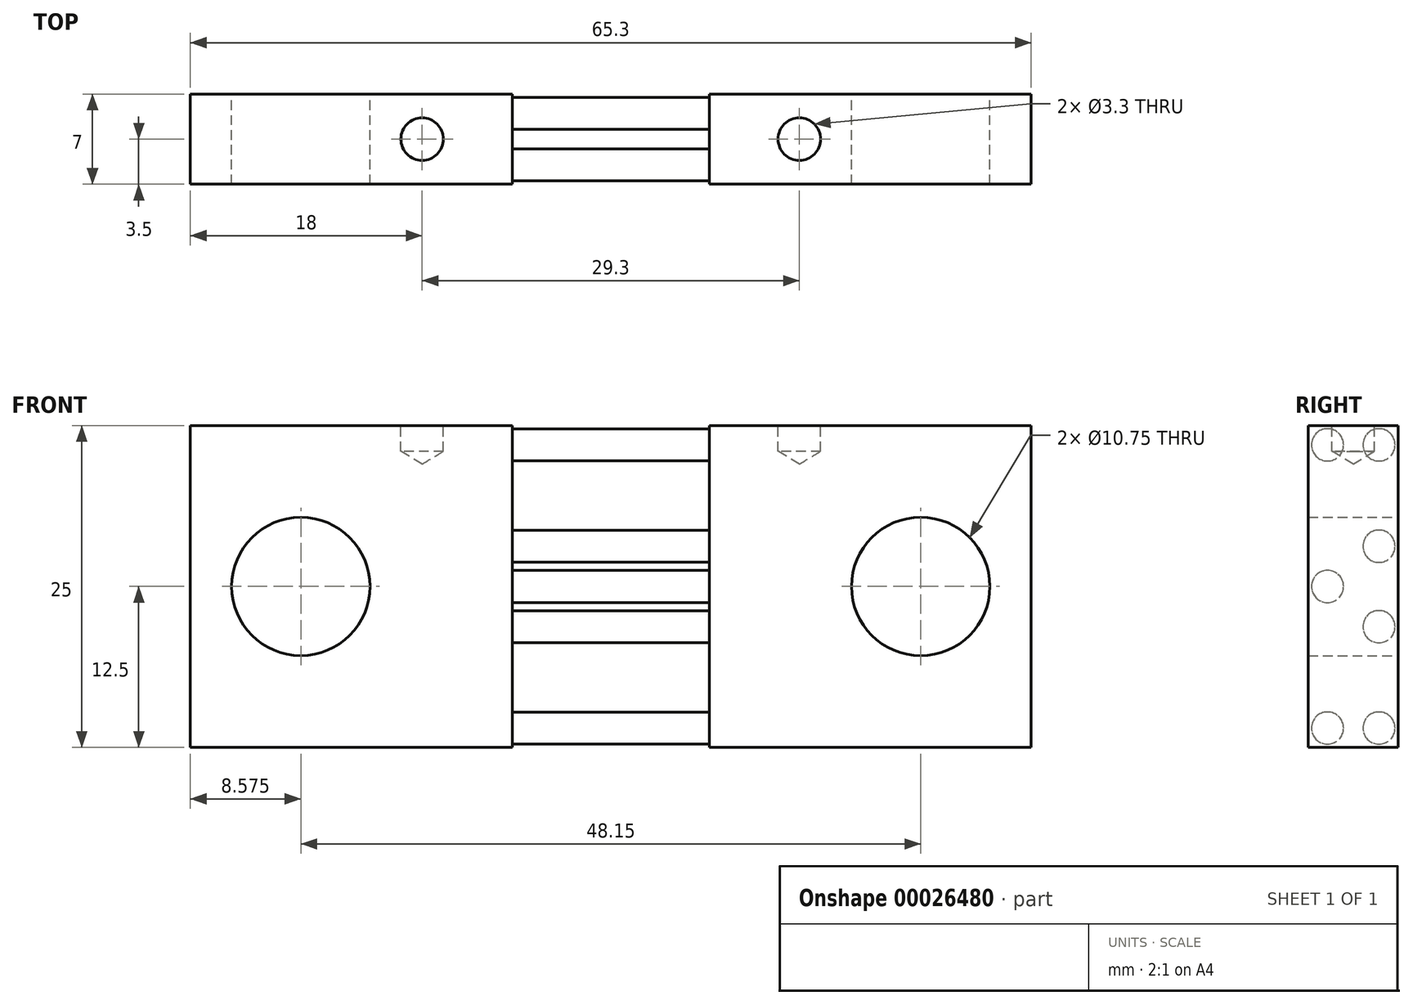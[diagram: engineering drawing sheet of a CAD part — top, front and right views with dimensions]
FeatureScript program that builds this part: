
annotation { "Feature Type Name" : "Feature", "Feature Type Description" : "" }
export const myFeature = defineFeature(function(context is Context, id is Id, definition is map)
    precondition{}
    {
        {
            var Q0;
            Q0=qCreatedBy(makeId("Front.planeOp"),FACE);
            var sketch = newSketch(context, id + "F0", { "sketchPlane" : qUnion([Q0])});
            skLineSegment(sketch, "E0.rect.bottom", {"start": v(-32.65, -12.5) * mm, "end": v(-7.65, -12.5) * mm});
            skLineSegment(sketch, "E0.rect.top", {"start": v(-32.65, 12.5) * mm, "end": v(-7.65, 12.5) * mm});
            skLineSegment(sketch, "E0.rect.left", {"start": v(-32.65, -12.5) * mm, "end": v(-32.65, 12.5) * mm});
            skLineSegment(sketch, "E0.rect.right", {"start": v(-7.65, -12.5) * mm, "end": v(-7.65, 12.5) * mm});
            skPoint(sketch, "E0.rect.middle", {"position": v(-20.15, 0) * mm});
            skLineSegment(sketch, "E1.rect.bottom", {"start": v(32.65, -12.5) * mm, "end": v(7.65, -12.5) * mm});
            skLineSegment(sketch, "E1.rect.top", {"start": v(32.65, 12.5) * mm, "end": v(7.65, 12.5) * mm});
            skLineSegment(sketch, "E1.rect.left", {"start": v(32.65, -12.5) * mm, "end": v(32.65, 12.5) * mm});
            skLineSegment(sketch, "E1.rect.right", {"start": v(7.65, -12.5) * mm, "end": v(7.65, 12.5) * mm});
            skPoint(sketch, "E1.rect.middle", {"position": v(20.15, 0) * mm});
            skLineSegment(sketch, "E2", {"start": v(-7.65, 12.5) * mm, "end": v(7.65, 12.5) * mm, "construction": true});
            skCircle(sketch, "E3", {"center": v(-24.07, 0) * mm, "radius": 5.38 * mm});
            skCircle(sketch, "E4", {"center": v(24.08, 0) * mm, "radius": 5.38 * mm});
            skSolve(sketch);
        }
        {
            var Q0;
            Q0=makeQuery(id+"F0.imprint","IMPRINT",FACE,{"disambiguationData":[TD([[makeQuery(id+"F0.imprint","IMPRINT",EDGE,{"derivedFrom":sQuery(id+"F0.wireOp",EDGE,"E0.rect.bottom")}),1.0]])]});
            var Q1;
            Q1=makeQuery(id+"F0.imprint","IMPRINT",FACE,{"disambiguationData":[TD([[makeQuery(id+"F0.imprint","IMPRINT",EDGE,{"derivedFrom":sQuery(id+"F0.wireOp",EDGE,"E1.rect.bottom")}),-1.0]])]});
            extrude(context, id + "F1", {"entities" : qUnion([Q0, Q1]), "endBound" : BoundingType.SYMMETRIC, "depth" : 7 * mm});
        }
        {
            var Q0;
            Q0=makeQuery(id+"F1.opExtrude","SWEPT_FACE",FACE,{"disambiguationData":[OSD([sQuery(id+"F0.wireOp",EDGE,"E0.rect.right")])]});
            var sketch = newSketch(context, id + "F2", { "sketchPlane" : qUnion([Q0])});
            skCircle(sketch, "E5", {"center": v(-2, 11) * mm, "radius": 1.25 * mm});
            skCircle(sketch, "E6", {"center": v(-2, 0) * mm, "radius": 1.25 * mm});
            skCircle(sketch, "E7", {"center": v(-2, -11) * mm, "radius": 1.25 * mm});
            skCircle(sketch, "E8", {"center": v(2, 11) * mm, "radius": 1.25 * mm});
            skCircle(sketch, "E9", {"center": v(2, 3.13) * mm, "radius": 1.25 * mm});
            skCircle(sketch, "E10", {"center": v(2, -3.12) * mm, "radius": 1.25 * mm});
            skCircle(sketch, "E11", {"center": v(2, -11) * mm, "radius": 1.25 * mm});
            skLineSegment(sketch, "E12", {"start": v(-3.5, 0) * mm, "end": v(3.5, 0) * mm, "construction": true});
            skSolve(sketch);
        }
        {
            var Q0;
            Q0=makeQuery(id+"F2.imprint","IMPRINT",FACE,{"disambiguationData":[TD([[makeQuery(id+"F2.imprint","IMPRINT",EDGE,{"derivedFrom":sQuery(id+"F2.wireOp",EDGE,"E5")}),1.0]])]});
            var Q1;
            Q1=makeQuery(id+"F2.imprint","IMPRINT",FACE,{"disambiguationData":[TD([[makeQuery(id+"F2.imprint","IMPRINT",EDGE,{"derivedFrom":sQuery(id+"F2.wireOp",EDGE,"E8")}),1.0]])]});
            var Q2;
            Q2=makeQuery(id+"F2.imprint","IMPRINT",FACE,{"disambiguationData":[TD([[makeQuery(id+"F2.imprint","IMPRINT",EDGE,{"derivedFrom":sQuery(id+"F2.wireOp",EDGE,"E9")}),1.0]])]});
            var Q3;
            Q3=makeQuery(id+"F2.imprint","IMPRINT",FACE,{"disambiguationData":[TD([[makeQuery(id+"F2.imprint","IMPRINT",EDGE,{"derivedFrom":sQuery(id+"F2.wireOp",EDGE,"E6")}),1.0]])]});
            var Q4;
            Q4=makeQuery(id+"F2.imprint","IMPRINT",FACE,{"disambiguationData":[TD([[makeQuery(id+"F2.imprint","IMPRINT",EDGE,{"derivedFrom":sQuery(id+"F2.wireOp",EDGE,"E10")}),1.0]])]});
            var Q5;
            Q5=makeQuery(id+"F2.imprint","IMPRINT",FACE,{"disambiguationData":[TD([[makeQuery(id+"F2.imprint","IMPRINT",EDGE,{"derivedFrom":sQuery(id+"F2.wireOp",EDGE,"E11")}),1.0]])]});
            var Q6;
            Q6=makeQuery(id+"F2.imprint","IMPRINT",FACE,{"disambiguationData":[TD([[makeQuery(id+"F2.imprint","IMPRINT",EDGE,{"derivedFrom":sQuery(id+"F2.wireOp",EDGE,"E7")}),1.0]])]});
            extrude(context, id + "F3", {"entities" : qUnion([Q0, Q1, Q2, Q3, Q4, Q5, Q6]), "operationType" : NewBodyOperationType.ADD, "endBound" : BoundingType.UP_TO_NEXT, "depth" : 25 * mm});
        }
        {
            var Q0;
            Q0=makeQuery(id+"F1.opExtrude","SWEPT_FACE",FACE,{"disambiguationData":[OSD([sQuery(id+"F0.wireOp",EDGE,"E0.rect.top")])]});
            var sketch = newSketch(context, id + "F4", { "sketchPlane" : qUnion([Q0])});
            skPoint(sketch, "E13", {"position": v(-14.65, 0) * mm});
            skPoint(sketch, "E14", {"position": v(14.65, 0) * mm});
            skSolve(sketch);
        }
        {
            var Q0;
            Q0=sQuery(id+"F4.wireOp",VERTEX,"E13");
            var Q1;
            Q1=sQuery(id+"F4.wireOp",VERTEX,"E14");
            var Q2;
            Q2=makeQuery(id+"F1.opExtrude","SWEPT_BODY",BODY,{"disambiguationData":[OSD([sQuery(id+"F0.wireOp",EDGE,"E0.rect.bottom"),sQuery(id+"F0.wireOp",EDGE,"E0.rect.top"),sQuery(id+"F0.wireOp",EDGE,"E0.rect.left"),sQuery(id+"F0.wireOp",EDGE,"E0.rect.right"),sQuery(id+"F0.wireOp",EDGE,"E3")])]});
            var Q3;
            Q3=makeQuery(id+"F1.opExtrude","SWEPT_BODY",BODY,{"disambiguationData":[OSD([sQuery(id+"F0.wireOp",EDGE,"E1.rect.bottom"),sQuery(id+"F0.wireOp",EDGE,"E1.rect.top"),sQuery(id+"F0.wireOp",EDGE,"E1.rect.left"),sQuery(id+"F0.wireOp",EDGE,"E1.rect.right"),sQuery(id+"F0.wireOp",EDGE,"E4")])]});
            hole(context, id + "F5", {"style" : HoleStyle.SIMPLE, "holeDiameter" : 3.3 * mm, "endStyle" : HoleEndStyle.BLIND, "holeDepth" : 2 * mm, "locations" : qUnion([Q0, Q1]), "scope" : qUnion([Q2, Q3])});
        }
    });
